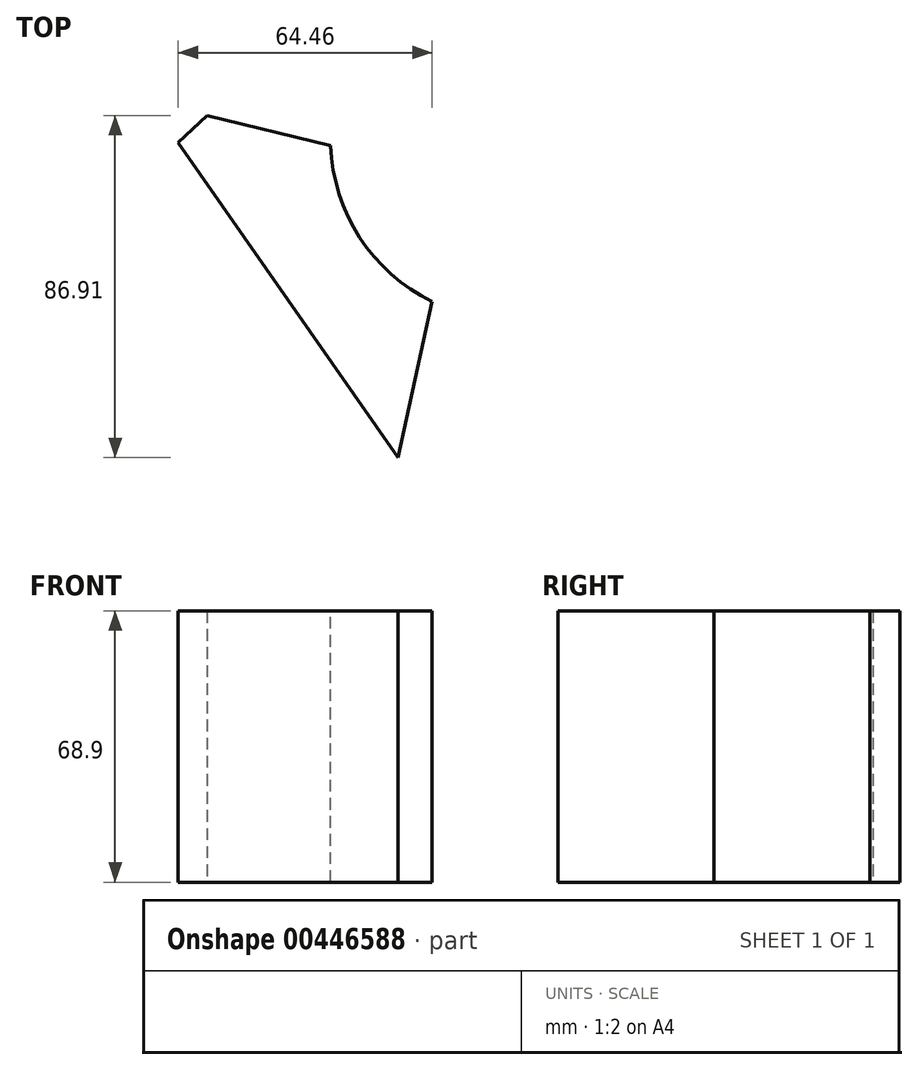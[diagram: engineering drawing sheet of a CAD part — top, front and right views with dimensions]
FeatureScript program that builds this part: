
annotation { "Feature Type Name" : "Feature", "Feature Type Description" : "" }
export const myFeature = defineFeature(function(context is Context, id is Id, definition is map)
    precondition{}
    {
        {
            var Q0;
            Q0=qCreatedBy(makeId("Top.planeOp"),FACE);
            var sketch = newSketch(context, id + "F0", { "sketchPlane" : qUnion([Q0])});
            skLineSegment(sketch, "E0", {"start": v(-41.36, 37.16) * mm, "end": v(14.52, -42.81) * mm});
            skLineSegment(sketch, "E1", {"start": v(14.52, -42.81) * mm, "end": v(29.96, 28.51) * mm});
            skLineSegment(sketch, "E2", {"start": v(29.96, 28.51) * mm, "end": v(-34.03, 44.1) * mm});
            skLineSegment(sketch, "E3", {"start": v(-34.03, 44.1) * mm, "end": v(-41.36, 37.16) * mm});
            skSolve(sketch);
        }
        {
            var Q0;
            Q0 = qSketchRegion(id + "F0", true);
            var Q1;
            Q1=makeQuery(id+"F0.imprint","IMPRINT",FACE,{"disambiguationData":[TD([[makeQuery(id+"F0.imprint","IMPRINT",EDGE,{"derivedFrom":sQuery(id+"F0.wireOp",EDGE,"E0")}),1.0]])]});
            extrude(context, id + "F1", {"entities" : qUnion([Q0, Q1]), "depth" : 68.9 * mm});
        }
        {
            var Q0;
            Q0=makeQuery(id+"F1.opExtrude","CAP_FACE",FACE,{"disambiguationData":[OSD([sQuery(id+"F0.wireOp",EDGE,"E0"),sQuery(id+"F0.wireOp",EDGE,"E1"),sQuery(id+"F0.wireOp",EDGE,"E2"),sQuery(id+"F0.wireOp",EDGE,"E3")])],"isStart":false});
            var sketch = newSketch(context, id + "F2", { "sketchPlane" : qUnion([Q0])});
            skCircle(sketch, "E4", {"center": v(43.44, 38.19) * mm, "radius": 46.1 * mm});
            skSolve(sketch);
        }
        {
            var Q0;
            Q0 = qSketchRegion(id + "F2", true);
            extrude(context, id + "F3", {"entities" : qUnion([Q0]), "operationType" : NewBodyOperationType.REMOVE, "oppositeDirection" : true, "depth" : 88.58 * mm});
        }
    });
